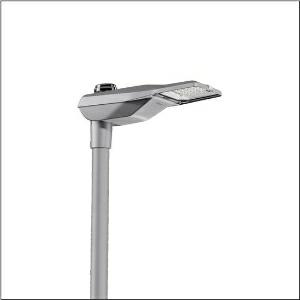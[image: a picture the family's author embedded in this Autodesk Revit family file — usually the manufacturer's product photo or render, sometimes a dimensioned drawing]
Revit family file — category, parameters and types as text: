
# Revit family: streetlight_sl_21_micro___st0_8a_5xe5c37n08db_0c9a
name_source: partatom
category: Lighting Fixtures
units: mm (PartAtom-declared; Revit-internal decimal feet)

## family parameters
Cut with Voids When Loaded = No
Host = Face
Light Source = No
Part Type = Normal
Room Calculation Point = No
Round Connector Dimension = Use Diameter
Shared = No

## types (1)
- --- (1 x LED, 5110 lm, 39.1 W, 3000K)
    Apparent Load = 39 VA
    CIE Flux Codes = 38 75 97 100 100
    Color Rendering = 70
    Color Temperature = 3000K
    Default Elevation = 1800 mm
    Description = Streetlight SL 21 micro, mast luminaire, primary light control with lens, of PMMA, primary optical cover: cover, of toughened safety glass, transparent, light distribution: ST0.8a, light emission: direct distribution, primary light characteristic: asymmetric, installation type: post-top, LED, 3G 1.5mm², High Power LED, rated luminous flux: 5.110lm, luminous efficacy: 131lm/W, light colour: 730, colour temperature: 3000K, control gear: NEMA (7pin), control: overheat protection, pre-setting: linear dimming characteristic, constant luminous flux control, time-dependent luminous flux control, flexible luminous flux parameterisation, mains connection: 230..240V, AC, 50/60Hz, connection cable pre-assembled, cable length: 6,5m, wiring characteristics: H07RN-F, start of lifetime: 39W, end of service life: 41W, reduction: 18W, luminaire housing, of diecast aluminium (EN AC-44300), powder-coated, SITECO metallic grey (DB 702S), corrosivity category C5 high according to DIN EN ISO 12944, multi-level sealing system, sealing non-destructively replaceable, inclination adjustable: 0°, 5°, 10°, 15°, length: 528mm, width: 235mm, height: 110mm, spigot size: 76/60mm (post-top), mounting height: 4..8m, protection rating (complete): IP66, insulation class (complete): insulation class I (protective earthing), certification: CE, ENEC, ENEC+, VDE, impact resistance: IK10, permissible operating ambient temperature for outdoor applications: -40..+50°C, standard-compliant lighting for roads and squares, packaging unit: 1 piece

Light Distribution: ST0.8a
    Height = 110 mm
    Lamp = 1 x LED
    Lamp Light Flux = 5110 lm
    Lamp Power = 39.1 W
    Lamp count = 1
    Length = 528 mm
    Luminous efficacy = 131 lm/W
    Manufacturer = Siteco
    ModVariant = No
    Model = 5XE5C37N08DB
    Number of Poles = 1
    OnlyDefault = Yes
    Power Factor = 1
    Product Name = Streetlight SL 21 micro | ST0.8a
    Product group = mast luminaire | pylon top
    ProductGroupID = 6100
    Protection Class = Protection class I
    Protection Degree = IP 66
    RLX_Detail_Level = 1
    RLX_Emergency_Light_Flux = 0 lm
    RLX_Emergency_Type = 0
    RLX_Emergency_Type_DB = No
    RlxData = <blob elided: 98849 chars, md5=693c47ac>
    Socket = socket
    Standby Power = 0 W
    System Light Flux = 5110 lm
    System Power = 39 W
    Type Comments = factory setting: luminous flux: 100 % | dim-lin: 254 | 765 mA
    Type Image = l_1294375.jpg
    URL = http://relux.com
    VarID = @adj_133869
    Voltage = 0 V
    Weight = 0.00 kg
    Width = 235 mm

## geometry (parser evidence)
native form markers: Blend x4, Sweep x9
no freeform markers — native parametric forms only
